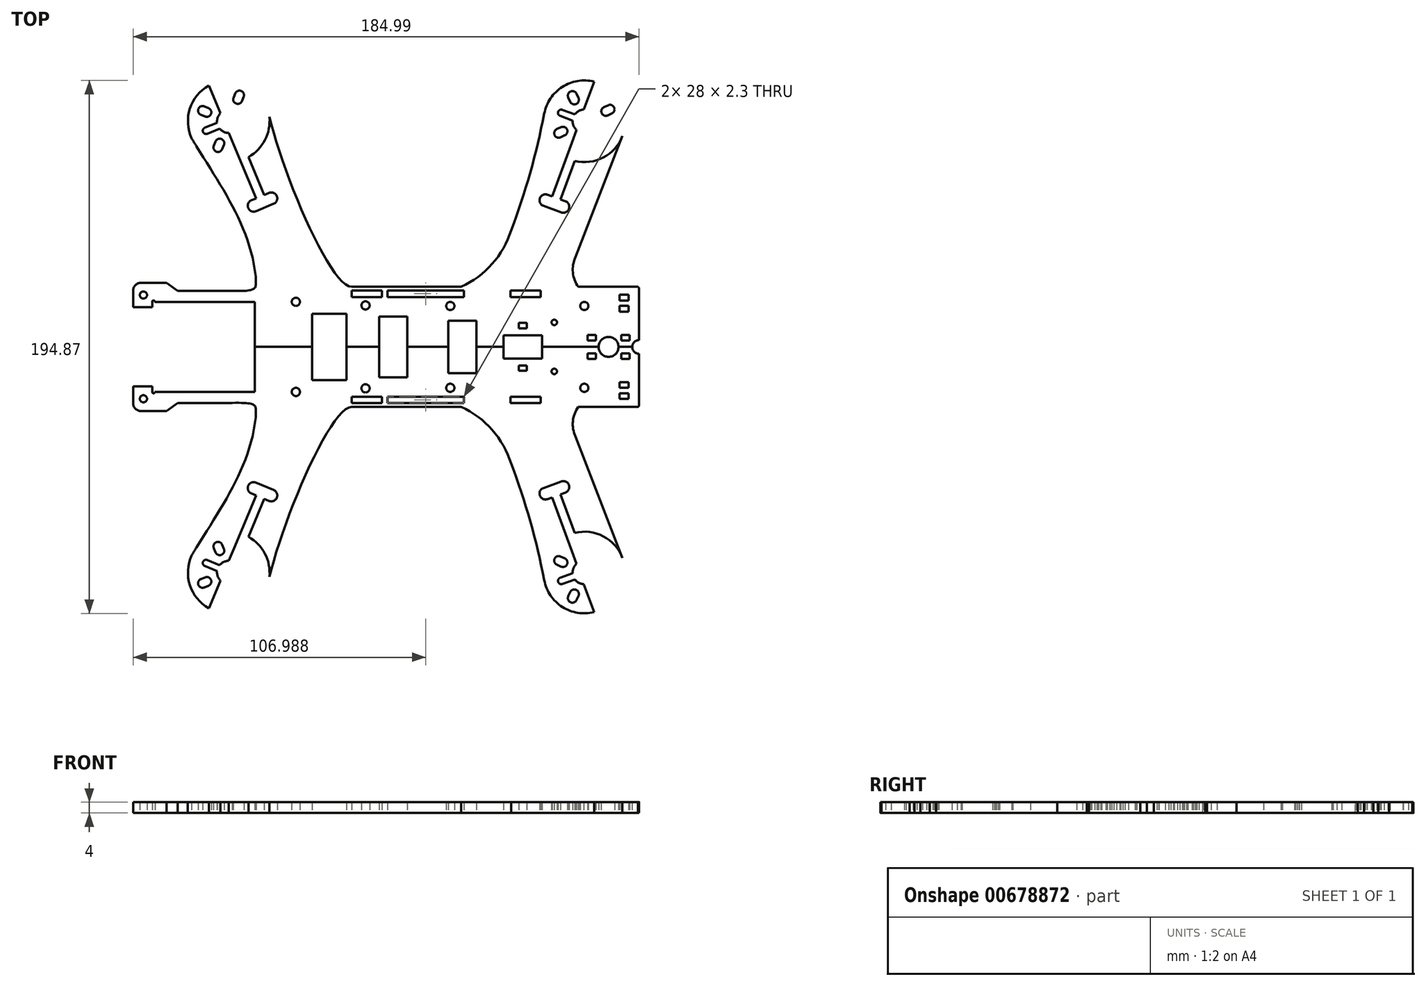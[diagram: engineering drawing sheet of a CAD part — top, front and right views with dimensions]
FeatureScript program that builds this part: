
annotation { "Feature Type Name" : "Feature", "Feature Type Description" : "" }
export const myFeature = defineFeature(function(context is Context, id is Id, definition is map)
    precondition{}
    {
        {
            var Q0;
            Q0=qCreatedBy(makeId("Top.planeOp"),FACE);
            var sketch = newSketch(context, id + "F0", { "sketchPlane" : qUnion([Q0])});
            skLineSegment(sketch, "E0.bottom", {"start": v(86.3, -10.98) * mm, "end": v(81.3, -10.98) * mm});
            skLineSegment(sketch, "E0.top", {"start": v(88.8, 10.98) * mm, "end": v(-16.2, 10.98) * mm});
            skLineSegment(sketch, "E0.left", {"start": v(88.8, -8.48) * mm, "end": v(88.8, 10.29) * mm});
            skArc(sketch, "E1", {"start": v(88.8, -8.48) * mm, "mid": v(87.04, -9.22) * mm, "end": v(86.3, -10.98) * mm});
            skLineSegment(sketch, "E2.bottom", {"start": v(81.69, 8.08) * mm, "end": v(84.96, 8.08) * mm});
            skLineSegment(sketch, "E2.top", {"start": v(81.69, 1.9) * mm, "end": v(84.96, 1.9) * mm});
            skLineSegment(sketch, "E2.left", {"start": v(81.69, 8.08) * mm, "end": v(81.69, 1.9) * mm});
            skLineSegment(sketch, "E2.right", {"start": v(84.96, 8.08) * mm, "end": v(84.96, 1.9) * mm});
            skArc(sketch, "E3", {"start": v(81.3, -10.98) * mm, "mid": v(77.66, -7.34) * mm, "end": v(74.02, -10.98) * mm});
            skLineSegment(sketch, "E4.trimOffspring", {"start": v(74.02, -10.98) * mm, "end": v(53.3, -10.98) * mm});
            skLineSegment(sketch, "E5.bottom", {"start": v(82.3, -6.62) * mm, "end": v(85.3, -6.62) * mm});
            skLineSegment(sketch, "E5.top", {"start": v(82.3, -8.62) * mm, "end": v(85.3, -8.62) * mm});
            skLineSegment(sketch, "E5.left", {"start": v(82.3, -6.62) * mm, "end": v(82.3, -8.62) * mm});
            skLineSegment(sketch, "E5.right", {"start": v(85.3, -6.62) * mm, "end": v(85.3, -8.62) * mm});
            skLineSegment(sketch, "E6.bottom", {"start": v(70.02, -6.62) * mm, "end": v(73.02, -6.62) * mm});
            skLineSegment(sketch, "E6.top", {"start": v(70.02, -8.62) * mm, "end": v(73.02, -8.62) * mm});
            skLineSegment(sketch, "E6.left", {"start": v(70.02, -6.62) * mm, "end": v(70.02, -8.62) * mm});
            skLineSegment(sketch, "E6.right", {"start": v(73.02, -6.62) * mm, "end": v(73.02, -8.62) * mm});
            skCircle(sketch, "E7", {"center": v(68.8, 3.98) * mm, "radius": 1.5 * mm});
            skCircle(sketch, "E8", {"center": v(57.8, -2.02) * mm, "radius": 1 * mm});
            skLineSegment(sketch, "E9.top", {"start": v(53.3, -6.72) * mm, "end": v(39.3, -6.72) * mm});
            skLineSegment(sketch, "E9.left", {"start": v(53.3, -10.98) * mm, "end": v(53.3, -6.72) * mm});
            skLineSegment(sketch, "E9.right", {"start": v(39.3, -10.98) * mm, "end": v(39.3, -6.72) * mm});
            skLineSegment(sketch, "E10.trimOffspring", {"start": v(39.3, -10.98) * mm, "end": v(29.3, -10.98) * mm});
            skLineSegment(sketch, "E11.bottom", {"start": v(47.8, -4.22) * mm, "end": v(44.8, -4.22) * mm});
            skLineSegment(sketch, "E11.top", {"start": v(47.8, -2.22) * mm, "end": v(44.8, -2.22) * mm});
            skLineSegment(sketch, "E11.left", {"start": v(47.8, -4.22) * mm, "end": v(47.8, -2.22) * mm});
            skLineSegment(sketch, "E11.right", {"start": v(44.8, -4.22) * mm, "end": v(44.8, -2.22) * mm});
            skPoint(sketch, "E11.middle", {"position": v(46.3, -3.22) * mm});
            skPoint(sketch, "E11.middle.positionSnap0", {"position": v(46.3, -6.72) * mm});
            skPoint(sketch, "E11.centerSnap0", {"position": v(46.3, -6.72) * mm});
            skPoint(sketch, "E12", {"position": v(23.8, 10.98) * mm});
            skArc(sketch, "E13", {"start": v(23.8, 10.98) * mm, "mid": v(35.12, 19.38) * mm, "end": v(42.05, 31.65) * mm});
            skArc(sketch, "E14", {"start": v(42.05, 31.65) * mm, "mid": v(49.33, 53.9) * mm, "end": v(54.6, 76.72) * mm});
            skArc(sketch, "E15", {"start": v(65.57, 21.8) * mm, "mid": v(64.61, 16.24) * mm, "end": v(66.62, 10.98) * mm});
            skArc(sketch, "E16", {"start": v(88.8, 10.26) * mm, "mid": v(88.7, 10.68) * mm, "end": v(88.4, 10.98) * mm});
            skPoint(sketch, "E17", {"position": v(-16.2, 10.98) * mm});
            skPoint(sketch, "E18", {"position": v(-24.2, 10.98) * mm});
            skLineSegment(sketch, "E19.top", {"start": v(29.3, -1.38) * mm, "end": v(19.09, -1.38) * mm});
            skLineSegment(sketch, "E19.left", {"start": v(29.3, -10.98) * mm, "end": v(29.3, -1.38) * mm});
            skLineSegment(sketch, "E19.right", {"start": v(19.09, -10.98) * mm, "end": v(19.09, -1.38) * mm});
            skLineSegment(sketch, "E20.top", {"start": v(4.09, 0.12) * mm, "end": v(-6.16, 0.12) * mm});
            skLineSegment(sketch, "E20.left", {"start": v(4.09, -10.98) * mm, "end": v(4.09, 0.12) * mm});
            skLineSegment(sketch, "E20.right", {"start": v(-6.16, -10.98) * mm, "end": v(-6.16, 0.12) * mm});
            skLineSegment(sketch, "E21.trimOffspring", {"start": v(19.09, -10.98) * mm, "end": v(4.09, -10.98) * mm});
            skLineSegment(sketch, "E22.trimOffspring", {"start": v(-6.16, -10.98) * mm, "end": v(-18.16, -10.98) * mm});
            skLineSegment(sketch, "E23.top", {"start": v(-18.16, 1.12) * mm, "end": v(-30.66, 1.12) * mm});
            skLineSegment(sketch, "E23.left", {"start": v(-18.16, -10.98) * mm, "end": v(-18.16, 1.12) * mm});
            skLineSegment(sketch, "E23.right", {"start": v(-30.66, -10.98) * mm, "end": v(-30.66, 1.12) * mm});
            skLineSegment(sketch, "E24.trimOffspring", {"start": v(-30.66, -10.98) * mm, "end": v(-51.68, -10.98) * mm});
            skLineSegment(sketch, "E25.bottom", {"start": v(-96.18, 5.48) * mm, "end": v(-89.18, 5.48) * mm});
            skLineSegment(sketch, "E25.right", {"start": v(-51.68, 5.48) * mm, "end": v(-51.68, -10.98) * mm});
            skLineSegment(sketch, "E26.top", {"start": v(-79.88, 9.48) * mm, "end": v(-59.88, 9.48) * mm});
            skLineSegment(sketch, "E27.top", {"start": v(-83.98, 12.48) * mm, "end": v(-93.23, 12.48) * mm});
            skLineSegment(sketch, "E28", {"start": v(-83.98, 12.48) * mm, "end": v(-79.88, 9.48) * mm});
            skLineSegment(sketch, "E29", {"start": v(-96.18, 9.53) * mm, "end": v(-96.18, 5.48) * mm});
            skFitSpline(sketch, "E30", {"points": [v(-59.88, 9.48) * mm, v(-51.31, 14.71) * mm], "startDerivative": vector(30, -0.45) * mm, "endDerivative": vector(0.33, 13.3) * mm});
            skLineSegment(sketch, "E31.top", {"start": v(-96.18, 3.48) * mm, "end": v(-89.18, 3.48) * mm});
            skLineSegment(sketch, "E31.left", {"start": v(-96.18, 5.48) * mm, "end": v(-96.18, 3.48) * mm});
            skLineSegment(sketch, "E31.right", {"start": v(-89.18, 5.48) * mm, "end": v(-89.18, 3.48) * mm});
            skPoint(sketch, "E32", {"position": v(-88.18, 5.48) * mm});
            skArc(sketch, "E33", {"start": v(-88.18, 5.48) * mm, "mid": v(-88.68, 5.98) * mm, "end": v(-89.18, 5.48) * mm});
            skLineSegment(sketch, "E34.trimOffspring", {"start": v(-88.18, 5.48) * mm, "end": v(-51.68, 5.48) * mm});
            skPoint(sketch, "E35", {"position": v(-93.18, 12.48) * mm});
            skPoint(sketch, "E36", {"position": v(-96.18, 9.48) * mm});
            skArc(sketch, "E37", {"start": v(-93.18, 12.48) * mm, "mid": v(-95.31, 11.61) * mm, "end": v(-96.18, 9.48) * mm});
            skPoint(sketch, "E38.orphan", {"position": v(-96.18, 12.48) * mm});
            skCircle(sketch, "E39", {"center": v(-92.38, 7.98) * mm, "radius": 1.3 * mm});
            skLineSegment(sketch, "E40.bottom", {"start": v(41.8, 9.58) * mm, "end": v(52.8, 9.58) * mm});
            skLineSegment(sketch, "E40.top", {"start": v(41.8, 7.28) * mm, "end": v(52.8, 7.28) * mm});
            skLineSegment(sketch, "E40.left", {"start": v(41.8, 9.58) * mm, "end": v(41.8, 7.28) * mm});
            skLineSegment(sketch, "E40.right", {"start": v(52.8, 9.58) * mm, "end": v(52.8, 7.28) * mm});
            skPoint(sketch, "E41.oppositeSnap0", {"position": v(41.8, 8.43) * mm});
            skLineSegment(sketch, "E42.bottom", {"start": v(-5.2, 9.58) * mm, "end": v(-16.2, 9.58) * mm});
            skLineSegment(sketch, "E42.top", {"start": v(-5.2, 7.28) * mm, "end": v(-16.2, 7.28) * mm});
            skLineSegment(sketch, "E42.left", {"start": v(-5.2, 9.58) * mm, "end": v(-5.2, 7.28) * mm});
            skLineSegment(sketch, "E42.right", {"start": v(-16.2, 9.58) * mm, "end": v(-16.2, 7.28) * mm});
            skLineSegment(sketch, "E43.bottom", {"start": v(-3.2, 9.58) * mm, "end": v(24.8, 9.58) * mm});
            skLineSegment(sketch, "E43.top", {"start": v(-3.2, 7.28) * mm, "end": v(24.8, 7.28) * mm});
            skLineSegment(sketch, "E43.left", {"start": v(-3.2, 9.58) * mm, "end": v(-3.2, 7.28) * mm});
            skLineSegment(sketch, "E43.right", {"start": v(24.8, 9.58) * mm, "end": v(24.8, 7.28) * mm});
            skCircle(sketch, "E44", {"center": v(19.8, 3.98) * mm, "radius": 1.5 * mm});
            skCircle(sketch, "E45", {"center": v(-36.66, 5.48) * mm, "radius": 1.5 * mm});
            skCircle(sketch, "E46", {"center": v(-11.18, 4.18) * mm, "radius": 1.5 * mm});
            skPoint(sketch, "E47", {"position": v(68.8, 71.52) * mm});
            skLineSegment(sketch, "E48", {"start": v(66.62, 10.98) * mm, "end": v(23.8, 10.98) * mm});
            skLineSegment(sketch, "E49", {"start": v(65.57, 21.8) * mm, "end": v(82.97, 66.73) * mm});
            skCircle(sketch, "E50", {"center": v(68.8, 71.52) * mm, "radius": 4.27 * mm});
            skCircle(sketch, "E51", {"center": v(68.8, 71.52) * mm, "radius": 14.93 * mm});
            skPoint(sketch, "E52", {"position": v(56.67, 63.42) * mm});
            skLineSegment(sketch, "E53.bottom", {"start": v(58.73, 68.64) * mm, "end": v(60.27, 69.36) * mm});
            skLineSegment(sketch, "E53.top", {"start": v(60.12, 65.65) * mm, "end": v(61.67, 66.36) * mm});
            skPoint(sketch, "E53.middle", {"position": v(60.2, 67.5) * mm});
            skPoint(sketch, "E54", {"position": v(61.67, 66.36) * mm});
            skArc(sketch, "E55", {"start": v(61.67, 66.36) * mm, "mid": v(62.52, 67.3) * mm, "end": v(62.46, 68.56) * mm});
            skArc(sketch, "E56.MirrorCS", {"start": v(60.27, 69.36) * mm, "mid": v(61.53, 69.41) * mm, "end": v(62.46, 68.56) * mm});
            skArc(sketch, "E57.MirrorCS", {"start": v(58.73, 68.64) * mm, "mid": v(57.88, 67.7) * mm, "end": v(57.93, 66.44) * mm});
            skArc(sketch, "E58.MirrorCS", {"start": v(60.12, 65.65) * mm, "mid": v(58.86, 65.6) * mm, "end": v(57.93, 66.44) * mm});
            skArc(sketch, "E59.MirrorCS", {"start": v(77.34, 73.68) * mm, "mid": v(76.08, 73.62) * mm, "end": v(75.15, 74.47) * mm});
            skPoint(sketch, "E60.MirrorP", {"position": v(77.42, 75.53) * mm});
            skLineSegment(sketch, "E61.MirrorCS", {"start": v(77.5, 77.39) * mm, "end": v(75.95, 76.67) * mm});
            skPoint(sketch, "E62.MirrorP", {"position": v(77.34, 73.68) * mm});
            skLineSegment(sketch, "E63.MirrorCS", {"start": v(78.89, 74.4) * mm, "end": v(77.34, 73.68) * mm});
            skArc(sketch, "E64.MirrorCS", {"start": v(77.5, 77.39) * mm, "mid": v(78.75, 77.44) * mm, "end": v(79.68, 76.59) * mm});
            skArc(sketch, "E65.MirrorCS", {"start": v(78.89, 74.4) * mm, "mid": v(79.74, 75.33) * mm, "end": v(79.68, 76.59) * mm});
            skArc(sketch, "E66.MirrorCS", {"start": v(75.95, 76.67) * mm, "mid": v(75.1, 75.74) * mm, "end": v(75.15, 74.47) * mm});
            skArc(sketch, "E67.MirrorCS", {"start": v(70.97, 62.98) * mm, "mid": v(70.91, 64.24) * mm, "end": v(71.77, 65.17) * mm});
            skPoint(sketch, "E68.MirrorP", {"position": v(72.68, 63.22) * mm});
            skLineSegment(sketch, "E69.MirrorCS", {"start": v(74.7, 62.8) * mm, "end": v(73.96, 64.37) * mm});
            skPoint(sketch, "E70.MirrorP", {"position": v(70.97, 62.98) * mm});
            skLineSegment(sketch, "E71.MirrorCS", {"start": v(71.69, 61.44) * mm, "end": v(70.97, 62.98) * mm});
            skArc(sketch, "E72.MirrorCS", {"start": v(74.68, 62.83) * mm, "mid": v(74.73, 61.57) * mm, "end": v(73.88, 60.64) * mm});
            skArc(sketch, "E73.MirrorCS", {"start": v(71.69, 61.44) * mm, "mid": v(72.62, 60.59) * mm, "end": v(73.88, 60.64) * mm});
            skArc(sketch, "E74.MirrorCS", {"start": v(73.96, 64.37) * mm, "mid": v(73.03, 65.23) * mm, "end": v(71.77, 65.17) * mm});
            skPoint(sketch, "E75.MirrorP", {"position": v(63.66, 78.66) * mm});
            skArc(sketch, "E76.MirrorCS", {"start": v(63.66, 78.66) * mm, "mid": v(64.59, 77.8) * mm, "end": v(65.85, 77.86) * mm});
            skPoint(sketch, "E77.MirrorP", {"position": v(64.94, 79.8) * mm});
            skArc(sketch, "E78.MirrorCS", {"start": v(66.65, 80.05) * mm, "mid": v(66.7, 78.8) * mm, "end": v(65.85, 77.86) * mm});
            skLineSegment(sketch, "E79.MirrorCS", {"start": v(62.94, 80.2) * mm, "end": v(63.66, 78.66) * mm});
            skLineSegment(sketch, "E80.MirrorCS", {"start": v(65.93, 81.6) * mm, "end": v(66.65, 80.05) * mm});
            skArc(sketch, "E81.MirrorCS", {"start": v(62.94, 80.2) * mm, "mid": v(62.88, 81.46) * mm, "end": v(63.74, 82.4) * mm});
            skArc(sketch, "E82.MirrorCS", {"start": v(65.93, 81.6) * mm, "mid": v(65, 82.45) * mm, "end": v(63.74, 82.4) * mm});
            skPoint(sketch, "E83.orphan", {"position": v(63.16, 67.06) * mm});
            skPoint(sketch, "E84.orphan", {"position": v(58.63, 64.95) * mm});
            skPoint(sketch, "E53.right.start.orphan", {"position": v(61.77, 70.05) * mm});
            skLineSegment(sketch, "E85", {"start": v(73.92, 85.55) * mm, "end": v(63.7, 57.48) * mm, "construction": true});
            skLineSegment(sketch, "E86", {"start": v(54.78, 76.62) * mm, "end": v(82.84, 66.4) * mm, "construction": true});
            skLineSegment(sketch, "E87", {"start": v(77.34, 73.68) * mm, "end": v(73.96, 64.37) * mm, "construction": true});
            skLineSegment(sketch, "E88", {"start": v(70.97, 62.98) * mm, "end": v(61.67, 66.36) * mm, "construction": true});
            skLineSegment(sketch, "E89", {"start": v(60.27, 69.36) * mm, "end": v(63.66, 78.66) * mm, "construction": true});
            skLineSegment(sketch, "E90", {"start": v(66.65, 80.05) * mm, "end": v(75.95, 76.67) * mm, "construction": true});
            skPoint(sketch, "E91", {"position": v(75.65, 69.02) * mm});
            skLineSegment(sketch, "E92", {"start": v(73.07, 71.23) * mm, "end": v(77.67, 69.56) * mm});
            skLineSegment(sketch, "E93", {"start": v(72.26, 69) * mm, "end": v(76.86, 67.32) * mm});
            skArc(sketch, "E94", {"start": v(76.86, 67.32) * mm, "mid": v(78.38, 68.03) * mm, "end": v(77.67, 69.56) * mm});
            skLineSegment(sketch, "E95.MirrorCS", {"start": v(64.54, 71.8) * mm, "end": v(59.94, 73.48) * mm});
            skLineSegment(sketch, "E96.MirrorCS", {"start": v(65.36, 74.04) * mm, "end": v(60.76, 75.71) * mm});
            skArc(sketch, "E97.MirrorCS", {"start": v(59.94, 73.48) * mm, "mid": v(59.23, 75) * mm, "end": v(60.76, 75.71) * mm});
            skPoint(sketch, "E98.MirrorP", {"position": v(61.96, 74) * mm});
            skLineSegment(sketch, "E99.MirrorCS", {"start": v(63.66, 78.66) * mm, "end": v(60.27, 69.36) * mm, "construction": true});
            skLineSegment(sketch, "E100.MirrorCS", {"start": v(82.84, 66.4) * mm, "end": v(54.78, 76.62) * mm, "construction": true});
            skLineSegment(sketch, "E101", {"start": v(71.7, 74.67) * mm, "end": v(73.36, 79.27) * mm});
            skLineSegment(sketch, "E102", {"start": v(68.63, 75.78) * mm, "end": v(70.3, 80.39) * mm});
            skArc(sketch, "E103", {"start": v(73.36, 79.27) * mm, "mid": v(72.4, 81.36) * mm, "end": v(70.3, 80.39) * mm});
            skLineSegment(sketch, "E104.MirrorCS", {"start": v(68.99, 67.25) * mm, "end": v(67.31, 62.65) * mm});
            skLineSegment(sketch, "E105.MirrorCS", {"start": v(65.93, 68.36) * mm, "end": v(64.25, 63.76) * mm});
            skLineSegment(sketch, "E106", {"start": v(70.3, 80.39) * mm, "end": v(72.35, 86.02) * mm});
            skLineSegment(sketch, "E107", {"start": v(73.36, 79.27) * mm, "end": v(75.42, 84.9) * mm});
            skLineSegment(sketch, "E108", {"start": v(64.25, 63.76) * mm, "end": v(62.2, 58.13) * mm});
            skLineSegment(sketch, "E109", {"start": v(67.31, 62.65) * mm, "end": v(65.26, 57.01) * mm});
            skPoint(sketch, "E110.orphan", {"position": v(67.31, 62.65) * mm});
            skPoint(sketch, "E111.MirrorCS.end.orphan", {"position": v(64.25, 63.76) * mm});
            skLineSegment(sketch, "E112", {"start": v(62.2, 58.13) * mm, "end": v(57.07, 44.03) * mm});
            skLineSegment(sketch, "E113", {"start": v(65.26, 57.01) * mm, "end": v(60.13, 42.92) * mm});
            skLineSegment(sketch, "E114", {"start": v(60.13, 42.92) * mm, "end": v(61.89, 42.28) * mm});
            skLineSegment(sketch, "E115", {"start": v(60.4, 38.2) * mm, "end": v(53.83, 40.6) * mm});
            skLineSegment(sketch, "E116", {"start": v(55.31, 44.67) * mm, "end": v(57.07, 44.03) * mm});
            skLineSegment(sketch, "E117", {"start": v(63.7, 57.48) * mm, "end": v(54.07, 31.02) * mm, "construction": true});
            skLineSegment(sketch, "E118", {"start": v(56.33, 42) * mm, "end": v(69.26, 37.3) * mm, "construction": true});
            skLineSegment(sketch, "E119", {"start": v(56.33, 42) * mm, "end": v(49.66, 44.42) * mm, "construction": true});
            skArc(sketch, "E120", {"start": v(60.4, 38.2) * mm, "mid": v(63.18, 39.5) * mm, "end": v(61.89, 42.28) * mm});
            skArc(sketch, "E121", {"start": v(55.31, 44.67) * mm, "mid": v(52.54, 43.38) * mm, "end": v(53.83, 40.6) * mm});
            skLineSegment(sketch, "E122", {"start": v(68.8, 71.52) * mm, "end": v(-115.4, 71.52) * mm, "construction": true});
            skPoint(sketch, "E123", {"position": v(-61.2, 71.52) * mm});
            skCircle(sketch, "E124", {"center": v(-61.2, 71.52) * mm, "radius": 4.27 * mm});
            skCircle(sketch, "E125", {"center": v(-61.2, 71.52) * mm, "radius": 14.93 * mm});
            skPoint(sketch, "E126", {"position": v(-64.64, 57.34) * mm});
            skLineSegment(sketch, "E127.bottom", {"start": v(-66.65, 62.57) * mm, "end": v(-66, 64.14) * mm});
            skLineSegment(sketch, "E127.top", {"start": v(-63.6, 61.32) * mm, "end": v(-62.95, 62.89) * mm});
            skPoint(sketch, "E127.middle", {"position": v(-64.8, 62.73) * mm});
            skPoint(sketch, "E128", {"position": v(-62.95, 62.89) * mm});
            skArc(sketch, "E129", {"start": v(-62.95, 62.89) * mm, "mid": v(-62.96, 64.15) * mm, "end": v(-63.85, 65.04) * mm});
            skArc(sketch, "E130.MirrorCS", {"start": v(-66, 64.14) * mm, "mid": v(-65.12, 65.04) * mm, "end": v(-63.85, 65.04) * mm});
            skArc(sketch, "E131.MirrorCS", {"start": v(-66.65, 62.57) * mm, "mid": v(-66.65, 61.3) * mm, "end": v(-65.75, 60.42) * mm});
            skArc(sketch, "E132.MirrorCS", {"start": v(-63.6, 61.32) * mm, "mid": v(-64.49, 60.42) * mm, "end": v(-65.75, 60.42) * mm});
            skArc(sketch, "E133.MirrorCS", {"start": v(-56.38, 78.89) * mm, "mid": v(-57.27, 78) * mm, "end": v(-58.53, 78) * mm});
            skPoint(sketch, "E134.MirrorP", {"position": v(-57.58, 80.3) * mm});
            skLineSegment(sketch, "E135.MirrorCS", {"start": v(-58.78, 81.72) * mm, "end": v(-59.43, 80.15) * mm});
            skPoint(sketch, "E136.MirrorP", {"position": v(-56.38, 78.89) * mm});
            skLineSegment(sketch, "E137.MirrorCS", {"start": v(-55.73, 80.46) * mm, "end": v(-56.38, 78.89) * mm});
            skArc(sketch, "E138.MirrorCS", {"start": v(-58.78, 81.72) * mm, "mid": v(-57.9, 82.61) * mm, "end": v(-56.63, 82.62) * mm});
            skArc(sketch, "E139.MirrorCS", {"start": v(-55.73, 80.46) * mm, "mid": v(-55.74, 81.72) * mm, "end": v(-56.63, 82.62) * mm});
            skArc(sketch, "E140.MirrorCS", {"start": v(-59.43, 80.15) * mm, "mid": v(-59.43, 78.88) * mm, "end": v(-58.53, 78) * mm});
            skArc(sketch, "E141.MirrorCS", {"start": v(-53.82, 66.7) * mm, "mid": v(-54.71, 67.6) * mm, "end": v(-54.72, 68.86) * mm});
            skPoint(sketch, "E142.MirrorP", {"position": v(-52.73, 68.04) * mm});
            skLineSegment(sketch, "E143.MirrorCS", {"start": v(-50.96, 69.1) * mm, "end": v(-52.56, 69.75) * mm});
            skPoint(sketch, "E144.MirrorP", {"position": v(-53.82, 66.7) * mm});
            skLineSegment(sketch, "E145.MirrorCS", {"start": v(-52.25, 66.06) * mm, "end": v(-53.82, 66.7) * mm});
            skArc(sketch, "E146.MirrorCS", {"start": v(-51, 69.1) * mm, "mid": v(-50.1, 68.22) * mm, "end": v(-50.1, 66.96) * mm});
            skArc(sketch, "E147.MirrorCS", {"start": v(-52.25, 66.06) * mm, "mid": v(-50.98, 66.06) * mm, "end": v(-50.1, 66.96) * mm});
            skArc(sketch, "E148.MirrorCS", {"start": v(-52.56, 69.75) * mm, "mid": v(-53.83, 69.75) * mm, "end": v(-54.72, 68.86) * mm});
            skPoint(sketch, "E149.MirrorP", {"position": v(-69.82, 73.28) * mm});
            skArc(sketch, "E150.MirrorCS", {"start": v(-69.82, 73.28) * mm, "mid": v(-68.56, 73.28) * mm, "end": v(-67.67, 74.18) * mm});
            skPoint(sketch, "E151.MirrorP", {"position": v(-69.66, 75) * mm});
            skArc(sketch, "E152.MirrorCS", {"start": v(-68.57, 76.33) * mm, "mid": v(-67.67, 75.44) * mm, "end": v(-67.67, 74.18) * mm});
            skLineSegment(sketch, "E153.MirrorCS", {"start": v(-71.4, 73.92) * mm, "end": v(-69.82, 73.28) * mm});
            skLineSegment(sketch, "E154.MirrorCS", {"start": v(-70.14, 76.98) * mm, "end": v(-68.57, 76.33) * mm});
            skArc(sketch, "E155.MirrorCS", {"start": v(-71.4, 73.92) * mm, "mid": v(-72.29, 74.81) * mm, "end": v(-72.3, 76.08) * mm});
            skArc(sketch, "E156.MirrorCS", {"start": v(-70.14, 76.98) * mm, "mid": v(-71.4, 76.97) * mm, "end": v(-72.3, 76.08) * mm});
            skPoint(sketch, "E157.orphan", {"position": v(-62.33, 64.41) * mm});
            skPoint(sketch, "E158.orphan", {"position": v(-64.23, 59.79) * mm});
            skPoint(sketch, "E127.right.start.orphan", {"position": v(-65.38, 65.67) * mm});
            skLineSegment(sketch, "E159", {"start": v(-66.94, 85.3) * mm, "end": v(-39.71, 20.07) * mm, "construction": true});
            skLineSegment(sketch, "E160", {"start": v(-74.97, 65.76) * mm, "end": v(-47.41, 77.27) * mm, "construction": true});
            skLineSegment(sketch, "E161", {"start": v(-56.38, 78.89) * mm, "end": v(-52.56, 69.75) * mm, "construction": true});
            skLineSegment(sketch, "E162", {"start": v(-53.82, 66.7) * mm, "end": v(-62.95, 62.89) * mm, "construction": true});
            skLineSegment(sketch, "E163", {"start": v(-66, 64.14) * mm, "end": v(-69.82, 73.28) * mm, "construction": true});
            skLineSegment(sketch, "E164", {"start": v(-68.57, 76.33) * mm, "end": v(-59.43, 80.15) * mm, "construction": true});
            skPoint(sketch, "E165", {"position": v(-54.47, 74.32) * mm});
            skLineSegment(sketch, "E166", {"start": v(-57.86, 74.2) * mm, "end": v(-53.35, 76.08) * mm});
            skLineSegment(sketch, "E167", {"start": v(-56.95, 72) * mm, "end": v(-52.43, 73.89) * mm});
            skArc(sketch, "E168", {"start": v(-52.43, 73.89) * mm, "mid": v(-51.79, 75.44) * mm, "end": v(-53.35, 76.08) * mm});
            skLineSegment(sketch, "E169.MirrorCS", {"start": v(-64.52, 68.84) * mm, "end": v(-69.04, 66.95) * mm});
            skLineSegment(sketch, "E170.MirrorCS", {"start": v(-65.44, 71.03) * mm, "end": v(-69.96, 69.15) * mm});
            skArc(sketch, "E171.MirrorCS", {"start": v(-69.04, 66.95) * mm, "mid": v(-70.6, 67.6) * mm, "end": v(-69.96, 69.15) * mm});
            skPoint(sketch, "E172.MirrorP", {"position": v(-67.91, 68.71) * mm});
            skLineSegment(sketch, "E173.MirrorCS", {"start": v(-69.82, 73.28) * mm, "end": v(-66, 64.14) * mm, "construction": true});
            skLineSegment(sketch, "E174.MirrorCS", {"start": v(-47.41, 77.27) * mm, "end": v(-74.97, 65.76) * mm, "construction": true});
            skLineSegment(sketch, "E175", {"start": v(-61.21, 75.79) * mm, "end": v(-63.1, 80.3) * mm});
            skLineSegment(sketch, "E176", {"start": v(-64.22, 74.53) * mm, "end": v(-66.1, 79.05) * mm});
            skArc(sketch, "E177", {"start": v(-63.1, 80.3) * mm, "mid": v(-65.23, 81.18) * mm, "end": v(-66.1, 79.05) * mm});
            skLineSegment(sketch, "E178.MirrorCS", {"start": v(-58.17, 68.5) * mm, "end": v(-56.28, 63.98) * mm});
            skLineSegment(sketch, "E179.MirrorCS", {"start": v(-61.17, 67.24) * mm, "end": v(-59.29, 62.72) * mm});
            skLineSegment(sketch, "E180", {"start": v(-66.1, 79.05) * mm, "end": v(-68.41, 84.59) * mm});
            skLineSegment(sketch, "E181", {"start": v(-63.1, 80.3) * mm, "end": v(-65.4, 85.84) * mm});
            skLineSegment(sketch, "E182", {"start": v(-59.29, 62.72) * mm, "end": v(-56.98, 57.2) * mm});
            skLineSegment(sketch, "E183", {"start": v(-56.28, 63.98) * mm, "end": v(-53.97, 58.45) * mm});
            skPoint(sketch, "E184.orphan", {"position": v(-56.28, 63.98) * mm});
            skPoint(sketch, "E185.MirrorCS.end.orphan", {"position": v(-59.29, 62.72) * mm});
            skLineSegment(sketch, "E186", {"start": v(-56.98, 57.2) * mm, "end": v(-51.2, 43.35) * mm});
            skLineSegment(sketch, "E187", {"start": v(-53.97, 58.45) * mm, "end": v(-48.2, 44.6) * mm});
            skLineSegment(sketch, "E188", {"start": v(-48.2, 44.6) * mm, "end": v(-46.46, 45.32) * mm});
            skLineSegment(sketch, "E189", {"start": v(-44.8, 41.33) * mm, "end": v(-51.26, 38.63) * mm});
            skLineSegment(sketch, "E190", {"start": v(-52.92, 42.63) * mm, "end": v(-51.2, 43.35) * mm});
            skLineSegment(sketch, "E191", {"start": v(-44.59, 31.75) * mm, "end": v(-39.71, 20.07) * mm, "construction": true});
            skLineSegment(sketch, "E192", {"start": v(-50.36, 41.35) * mm, "end": v(-37.67, 46.65) * mm, "construction": true});
            skLineSegment(sketch, "E193", {"start": v(-50.36, 41.35) * mm, "end": v(-56.92, 38.62) * mm, "construction": true});
            skArc(sketch, "E194", {"start": v(-44.8, 41.33) * mm, "mid": v(-43.63, 44.16) * mm, "end": v(-46.46, 45.32) * mm});
            skArc(sketch, "E195", {"start": v(-52.92, 42.63) * mm, "mid": v(-54.09, 39.8) * mm, "end": v(-51.26, 38.63) * mm});
            skLineSegment(sketch, "E196", {"start": v(-16.2, 10.98) * mm, "end": v(-47.68, 77.88) * mm, "construction": true});
            skLineSegment(sketch, "E197", {"start": v(-51.31, 14.71) * mm, "end": v(-74.74, 65.23) * mm, "construction": true});
            skFitSpline(sketch, "E198", {"points": [v(-74.74, 65.23) * mm, v(-51.31, 14.71) * mm], "startDerivative": vector(30.3, -50.3) * mm, "endDerivative": vector(6.34, -57.22) * mm});
            skFitSpline(sketch, "E199", {"points": [v(-46.34, 73.1) * mm, v(-16.2, 10.98) * mm], "startDerivative": vector(15.51, -63.48) * mm, "endDerivative": vector(24, 0) * mm});
            skLineSegment(sketch, "E200", {"start": v(81.69, 5) * mm, "end": v(84.96, 5) * mm, "construction": true});
            skLineSegment(sketch, "E201.bottom", {"start": v(84.96, 5.98) * mm, "end": v(81.69, 5.98) * mm});
            skLineSegment(sketch, "E201.top", {"start": v(84.96, 4) * mm, "end": v(81.69, 4) * mm});
            skLineSegment(sketch, "E201.left", {"start": v(84.96, 5.98) * mm, "end": v(84.96, 4) * mm});
            skLineSegment(sketch, "E201.right", {"start": v(81.69, 5.98) * mm, "end": v(81.69, 4) * mm});
            skPoint(sketch, "E201.middle", {"position": v(83.32, 5) * mm});
            skSolve(sketch);
        }
        {
            var Q0;
            {var subQ8=sQuery(id+"F0.wireOp",EDGE,"E13");Q0=makeQuery(id+"F0.imprint","IMPRINT",FACE,{"disambiguationData":[TD([[makeQuery(id+"F0.imprint","IMPRINT",EDGE,{"derivedFrom":subQ8}),-1.0]])]});}
            var Q1;
            Q1=makeQuery(id+"F0.imprint","IMPRINT",FACE,{"disambiguationData":[TD([[makeQuery(id+"F0.imprint","IMPRINT",EDGE,{"derivedFrom":sQuery(id+"F0.wireOp",EDGE,"E0.bottom")}),-1.0]])]});
            var Q2;
            Q2=makeQuery(id+"F0.imprint","IMPRINT",FACE,{"disambiguationData":[TD([[makeQuery(id+"F0.imprint","IMPRINT",EDGE,{"derivedFrom":sQuery(id+"F0.wireOp",EDGE,"E25.bottom")}),-1.0]])]});
            var Q3;
            Q3=makeQuery(id+"F0.imprint","IMPRINT",FACE,{"disambiguationData":[TD([[makeQuery(id+"F0.imprint","IMPRINT",EDGE,{"derivedFrom":sQuery(id+"F0.wireOp",EDGE,"beb36462-d6c1-41d3-b51b-f8d966d22955.bottom")}),1.0]])]});
            var Q4;
            Q4=makeQuery(id+"F0.imprint","IMPRINT",FACE,{"disambiguationData":[TD([[makeQuery(id+"F0.imprint","IMPRINT",EDGE,{"derivedFrom":sQuery(id+"F0.wireOp",EDGE,"E59.MirrorCS")}),1.0]])]});
            var Q5;
            Q5=makeQuery(id+"F0.imprint","IMPRINT",FACE,{"disambiguationData":[TD([[makeQuery(id+"F0.imprint","IMPRINT",EDGE,{"derivedFrom":sQuery(id+"F0.wireOp",EDGE,"E53.bottom")}),1.0]])]});
            var Q6;
            Q6=makeQuery(id+"F0.imprint","IMPRINT",FACE,{"disambiguationData":[TD([[makeQuery(id+"F0.imprint","IMPRINT",EDGE,{"derivedFrom":sQuery(id+"F0.wireOp",EDGE,"E133.MirrorCS")}),1.0]])]});
            var Q7;
            Q7=makeQuery(id+"F0.imprint","IMPRINT",FACE,{"disambiguationData":[TD([[makeQuery(id+"F0.imprint","IMPRINT",EDGE,{"derivedFrom":sQuery(id+"F0.wireOp",EDGE,"E127.bottom")}),1.0]])]});
            var Q8;
            Q8=makeQuery(id+"F0.imprint","IMPRINT",FACE,{"disambiguationData":[TD([[makeQuery(id+"F0.imprint","IMPRINT",EDGE,{"derivedFrom":sQuery(id+"F0.wireOp",EDGE,"E201.bottom")}),1.0]])]});
            extrude(context, id + "F1", {"entities" : qUnion([Q0, Q1, Q2, Q3, Q4, Q5, Q6, Q7, Q8]), "depth" : 4 * mm, "offsetDistance" : 25 * mm});
        }
        {
            var Q0;
            Q0=makeQuery(id+"F1.opExtrude","SWEPT_BODY",BODY,{"disambiguationData":[OSD([sQuery(id+"F0.wireOp",EDGE,"E0.bottom"),sQuery(id+"F0.wireOp",EDGE,"E0.top"),sQuery(id+"F0.wireOp",EDGE,"E0.left"),sQuery(id+"F0.wireOp",EDGE,"E0.right"),sQuery(id+"F0.wireOp",EDGE,"E1"),sQuery(id+"F0.wireOp",EDGE,"E2.bottom"),sQuery(id+"F0.wireOp",EDGE,"E2.top"),sQuery(id+"F0.wireOp",EDGE,"E2.left"),sQuery(id+"F0.wireOp",EDGE,"E2.right"),sQuery(id+"F0.wireOp",EDGE,"E3"),sQuery(id+"F0.wireOp",EDGE,"E4.trimOffspring"),sQuery(id+"F0.wireOp",EDGE,"E5.bottom"),sQuery(id+"F0.wireOp",EDGE,"E5.top"),sQuery(id+"F0.wireOp",EDGE,"E5.left"),sQuery(id+"F0.wireOp",EDGE,"E5.right"),sQuery(id+"F0.wireOp",EDGE,"E6.bottom"),sQuery(id+"F0.wireOp",EDGE,"E6.top"),sQuery(id+"F0.wireOp",EDGE,"E6.left"),sQuery(id+"F0.wireOp",EDGE,"E6.right"),sQuery(id+"F0.wireOp",EDGE,"E7"),sQuery(id+"F0.wireOp",EDGE,"E8"),sQuery(id+"F0.wireOp",EDGE,"E9.top"),sQuery(id+"F0.wireOp",EDGE,"E9.left"),sQuery(id+"F0.wireOp",EDGE,"E9.right"),sQuery(id+"F0.wireOp",EDGE,"E10.trimOffspring"),sQuery(id+"F0.wireOp",EDGE,"E11.bottom"),sQuery(id+"F0.wireOp",EDGE,"E11.top"),sQuery(id+"F0.wireOp",EDGE,"E11.left"),sQuery(id+"F0.wireOp",EDGE,"E11.right"),sQuery(id+"F0.wireOp",EDGE,"Rkiego0c-gQwe-95Ua-QFmb-WnrheuLpRx8P"),sQuery(id+"F0.wireOp",EDGE,"c2Eb3TdQ-ayrf-ccjF-HIVO-0mZij4ANF6hd"),sQuery(id+"F0.wireOp",EDGE,"E13"),sQuery(id+"F0.wireOp",EDGE,"E14"),sQuery(id+"F0.wireOp",EDGE,"E15"),sQuery(id+"F0.wireOp",EDGE,"rO4glKsI-mLVn-fgsM-m3i1-zsKFJTR3m1LZ"),sQuery(id+"F0.wireOp",EDGE,"W29Rnyu2-5tTr-r3EB-3rMK-oCu7kYDfpNRN"),sQuery(id+"F0.wireOp",EDGE,"E16"),sQuery(id+"F0.wireOp",EDGE,"t2mIQUEO-il6O-z1Le-362X-W5dMV7iqN6GU"),sQuery(id+"F0.wireOp",EDGE,"ytRxB9SY-fefi-0kDp-GV90-TIB4xOeh80wU"),sQuery(id+"F0.wireOp",EDGE,"2ca77470-bc45-4dfc-a7ba-68567e348b1c"),sQuery(id+"F0.wireOp",EDGE,"911afa97-74fd-434c-985a-d69e5bcfd5cb"),sQuery(id+"F0.wireOp",EDGE,"E19.top"),sQuery(id+"F0.wireOp",EDGE,"E19.left"),sQuery(id+"F0.wireOp",EDGE,"E19.right"),sQuery(id+"F0.wireOp",EDGE,"E20.top"),sQuery(id+"F0.wireOp",EDGE,"E20.left"),sQuery(id+"F0.wireOp",EDGE,"E20.right"),sQuery(id+"F0.wireOp",EDGE,"E21.trimOffspring")])]});
            var Q1;
            Q1=makeQuery(id+"F1.opExtrude","SWEPT_FACE",FACE,{"disambiguationData":[OSD([sQuery(id+"F0.wireOp",EDGE,"E0.bottom")])]});
            mirror(context, id + "F2", {"operationType" : NewBodyOperationType.ADD, "entities" : qUnion([Q0]), "mirrorPlane" : qUnion([Q1])});
        }
    });
